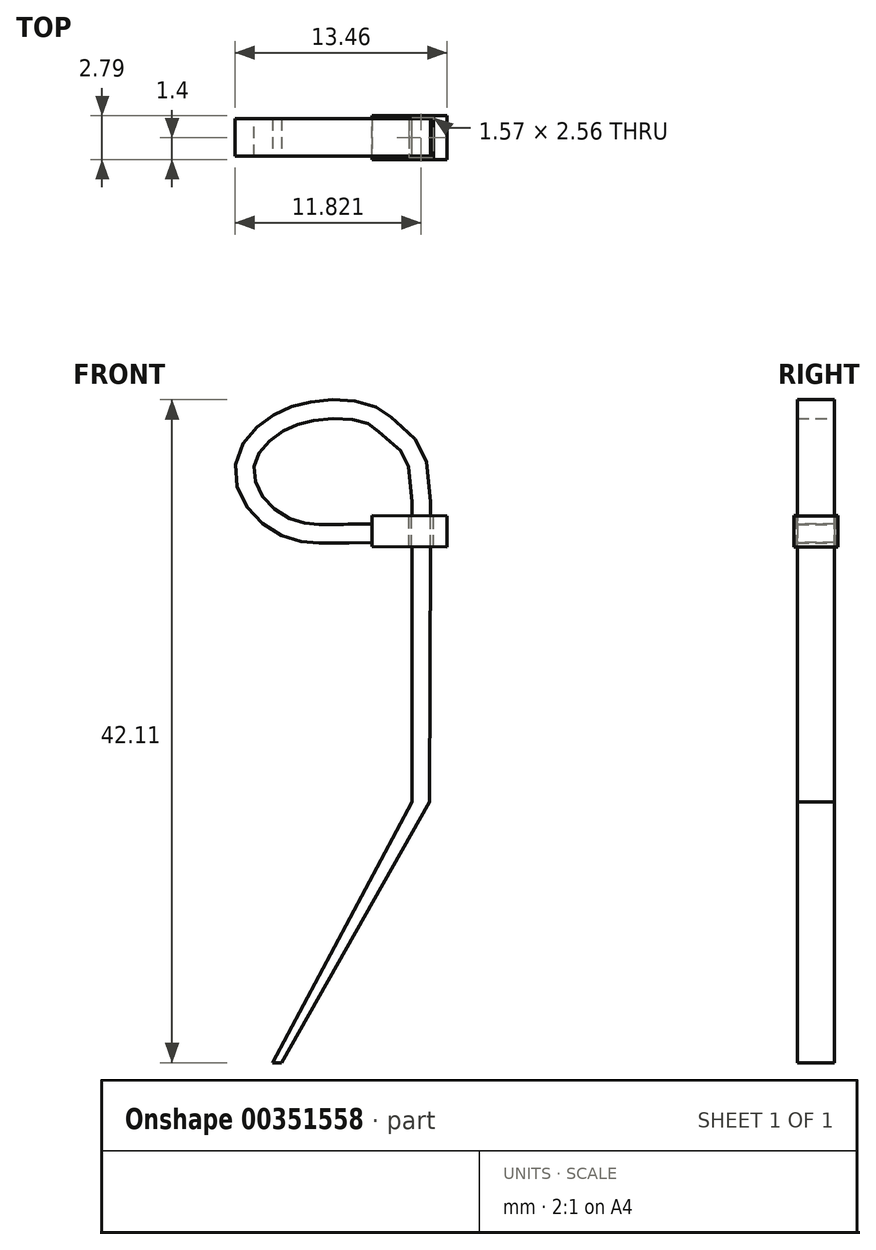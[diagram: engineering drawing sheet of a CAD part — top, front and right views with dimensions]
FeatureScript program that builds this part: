
annotation { "Feature Type Name" : "Feature", "Feature Type Description" : "" }
export const myFeature = defineFeature(function(context is Context, id is Id, definition is map)
    precondition{}
    {
        {
            var Q0;
            Q0=qCreatedBy(makeId("Top.planeOp"),FACE);
            var sketch = newSketch(context, id + "F0", { "sketchPlane" : qUnion([Q0])});
            skLineSegment(sketch, "E0.bottom", {"start": v(-0.6, 1.2) * mm, "end": v(0.6, 1.2) * mm});
            skLineSegment(sketch, "E0.top", {"start": v(-0.6, -1.2) * mm, "end": v(0.6, -1.2) * mm});
            skLineSegment(sketch, "E0.left", {"start": v(-0.6, 1.2) * mm, "end": v(-0.6, -1.2) * mm});
            skLineSegment(sketch, "E0.right", {"start": v(0.6, 1.2) * mm, "end": v(0.6, -1.2) * mm});
            skPoint(sketch, "E0.middle", {"position": v(0, 0) * mm});
            skSolve(sketch);
        }
        {
            var Q0;
            Q0=qCreatedBy(makeId("Front.planeOp"),FACE);
            var sketch = newSketch(context, id + "F1", { "sketchPlane" : qUnion([Q0])});
            skLineSegment(sketch, "E1", {"start": v(0, 0) * mm, "end": v(0, 19.05) * mm});
            skLineSegment(sketch, "E2", {"start": v(0, 19.05) * mm, "end": v(-25.4, 19.05) * mm, "construction": true});
            skFitSpline(sketch, "E3", {"points": [v(0, 19.05) * mm, v(-1.7, 23.42) * mm, v(-3.28, 24.61) * mm, v(-6.69, 24.85) * mm, v(-9.25, 23.95) * mm, v(-11.12, 21.82) * mm, v(-10.58, 19.05) * mm, v(-7.98, 17.22) * mm, v(-5.87, 17.03) * mm, v(-4.91, 17.02) * mm, v(-3.14, 17.05) * mm], "startDerivative": vector(0, 73.06) * mm, "endDerivative": vector(62.58, -0.29) * mm});
            skSolve(sketch);
        }
        {
            var Q0;
            Q0=makeQuery(id+"F0.imprint","IMPRINT",FACE,{"disambiguationData":[TD([[makeQuery(id+"F0.imprint","IMPRINT",EDGE,{"derivedFrom":sQuery(id+"F0.wireOp",EDGE,"E0.bottom")}),-1.0]])]});
            var Q1;
            Q1 = qConstructionFilter(qBodyType(qCreatedBy(id + "F1" ,EDGE), BodyType.WIRE), ConstructionObject.NO);
            sweep(context, id + "F2", {"profiles" : qUnion([Q0]), "path" : qUnion([Q1])});
        }
        {
            var Q0;
            Q0=makeQuery(id+"F2.opSweep","CAP_FACE",FACE,{"disambiguationData":[OSD([sQuery(id+"F0.wireOp",EDGE,"E0.bottom"),sQuery(id+"F0.wireOp",EDGE,"E0.top"),sQuery(id+"F0.wireOp",EDGE,"E0.left"),sQuery(id+"F0.wireOp",EDGE,"E0.right"),sQuery(id+"F1.wireOp",VERTEX,"E3.end")])],"isStart":false});
            var sketch = newSketch(context, id + "F3", { "sketchPlane" : qUnion([Q0])});
            skLineSegment(sketch, "E4.bottom", {"start": v(-1.4, 16.2) * mm, "end": v(1.4, 16.2) * mm});
            skLineSegment(sketch, "E4.top", {"start": v(-1.4, 18.17) * mm, "end": v(1.4, 18.17) * mm});
            skLineSegment(sketch, "E4.left", {"start": v(-1.4, 16.2) * mm, "end": v(-1.4, 18.17) * mm});
            skLineSegment(sketch, "E4.right", {"start": v(1.4, 16.2) * mm, "end": v(1.4, 18.17) * mm});
            skSolve(sketch);
        }
        {
            var Q0;
            Q0 = qSketchRegion(id + "F3", true);
            extrude(context, id + "F4", {"entities" : qUnion([Q0]), "operationType" : NewBodyOperationType.ADD, "depth" : 4.76 * mm});
        }
        {
            var Q0;
            Q0=makeQuery(id+"F4.opExtrude","SWEPT_FACE",FACE,{"disambiguationData":[OSD([sQuery(id+"F3.wireOp",EDGE,"E4.top")])]});
            var sketch = newSketch(context, id + "F5", { "sketchPlane" : qUnion([Q0])});
            skLineSegment(sketch, "E5.bottom", {"start": v(-0.87, 1.28) * mm, "end": v(0.7, 1.28) * mm});
            skLineSegment(sketch, "E5.top", {"start": v(-0.87, -1.28) * mm, "end": v(0.7, -1.28) * mm});
            skLineSegment(sketch, "E5.left", {"start": v(-0.87, 1.28) * mm, "end": v(-0.87, -1.28) * mm});
            skLineSegment(sketch, "E5.right", {"start": v(0.7, 1.28) * mm, "end": v(0.7, -1.28) * mm});
            skPoint(sketch, "E5.middle", {"position": v(-0.08, 0) * mm});
            skLineSegment(sketch, "E6.bottom", {"start": v(-0.79, 1.2) * mm, "end": v(0.62, 1.2) * mm});
            skLineSegment(sketch, "E6.top", {"start": v(-0.79, -1.2) * mm, "end": v(0.62, -1.2) * mm});
            skLineSegment(sketch, "E7", {"start": v(-0.71, 1.2) * mm, "end": v(-0.71, -1.2) * mm});
            skLineSegment(sketch, "E8", {"start": v(0.51, 1.2) * mm, "end": v(0.51, -1.2) * mm});
            skSolve(sketch);
        }
        {
            var Q0;
            Q0=makeQuery(id+"F5.imprint","IMPRINT",FACE,{"disambiguationData":[TD([[makeQuery(id+"F5.imprint","IMPRINT",EDGE,{"derivedFrom":sQuery(id+"F5.wireOp",EDGE,"E5.bottom")}),-1.0]])]});
            extrude(context, id + "F6", {"entities" : qUnion([Q0]), "operationType" : NewBodyOperationType.REMOVE, "oppositeDirection" : true, "depth" : 25.4 * mm});
        }
        {
            var Q0;
            Q0=qCreatedBy(makeId("Front.planeOp"),FACE);
            var sketch = newSketch(context, id + "F7", { "sketchPlane" : qUnion([Q0])});
            skLineSegment(sketch, "E9", {"start": v(0, 0) * mm, "end": v(-9.4, -16.57) * mm});
            skSolve(sketch);
        }
        {
            var Q0;
            Q0=makeQuery(id+"F2.opSweep","CAP_FACE",FACE,{"disambiguationData":[OSD([sQuery(id+"F0.wireOp",EDGE,"E0.bottom"),sQuery(id+"F0.wireOp",EDGE,"E0.top"),sQuery(id+"F0.wireOp",EDGE,"E0.left"),sQuery(id+"F0.wireOp",EDGE,"E0.right"),sQuery(id+"F1.wireOp",VERTEX,"E1.start")])],"isStart":true});
            var Q1;
            Q1=sQuery(id+"F7.wireOp",EDGE,"E9");
            sweep(context, id + "F8", {"operationType" : NewBodyOperationType.ADD, "profiles" : qUnion([Q0]), "path" : qUnion([Q1])});
        }
        {
            var Q0;
            {var subQ0=sQuery(id+"F1.wireOp",VERTEX,"E1.start");var subQ1=sQuery(id+"F0.wireOp",EDGE,"E0.top");var subQ4=sQuery(id+"F1.wireOp",EDGE,"E1");var subQ7=sQuery(id+"F3.wireOp",EDGE,"E4.bottom");var subQ8=makeQuery(id+"F2.opSweep","SWEPT_FACE",FACE,{"disambiguationData":[OSD([subQ1,subQ4])]});var subQ10=sQuery(id+"F3.wireOp",EDGE,"E4.top");Q0=makeQuery(id+"F8.boolean.opBoolean","MERGE",FACE,{"derivedFrom":[makeQuery(id+"F6.boolean.opBoolean","MERGE",FACE,{"derivedFrom":[makeQuery(id+"F4.boolean.opBoolean","SPLIT",FACE,{"disambiguationData":[TD([makeQuery(id+"F4.opExtrude","SWEPT_FACE",FACE,{"disambiguationData":[OSD([subQ10])]})])],"derivedFrom":subQ8}),makeQuery(id+"F4.boolean.opBoolean","SPLIT",FACE,{"disambiguationData":[TD([makeQuery(id+"F4.opExtrude","SWEPT_FACE",FACE,{"disambiguationData":[OSD([subQ7])]})])],"derivedFrom":subQ8}),makeQuery(id+"F6.opExtrude","SWEPT_FACE",FACE,{"disambiguationData":[OSD([sQuery(id+"F5.wireOp",EDGE,"E6.top")])]})]}),makeQuery(id+"F8.opSweep","SWEPT_FACE",FACE,{"disambiguationData":[OSD([subQ1,subQ0,sQuery(id+"F7.wireOp",EDGE,"E9")])]})]});}
            var sketch = newSketch(context, id + "F9", { "sketchPlane" : qUnion([Q0])});
            skLineSegment(sketch, "E10", {"start": v(-0.6, 0) * mm, "end": v(-9.44, -16.57) * mm});
            skLineSegment(sketch, "E11", {"start": v(-9.44, -16.57) * mm, "end": v(-10, -16.57) * mm});
            skLineSegment(sketch, "E12", {"start": v(-10, -16.57) * mm, "end": v(-0.6, 0) * mm});
            skSolve(sketch);
        }
        {
            var Q0;
            Q0 = qSketchRegion(id + "F9", true);
            extrude(context, id + "F10", {"entities" : qUnion([Q0]), "operationType" : NewBodyOperationType.REMOVE, "oppositeDirection" : true, "depth" : 25.4 * mm});
        }
    });
